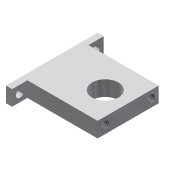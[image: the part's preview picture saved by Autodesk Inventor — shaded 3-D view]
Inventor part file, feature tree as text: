
AUTODESK INVENTOR PART (.ipt)
format: ipt  version: 2014 SP2 (Build 180246200, 246)  size: 131,072 bytes
history: native  units: in
note: dims shown in document units (in); Inventor stores cm internally (conversion verified against a paired STEP export)
features: extrude x7, sketch x7, thread x2
ambient origin geometry x8: Origin, YZ Plane, XZ Plane, XY Plane, X Axis, Y Axis, Z Axis, Center Point
bodies: Solid1 (feature_tree)
feature tree (16):
  extrude  "Extrusion1"  Depth=2.0in
  extrude  "Extrusion3"  Depth=0.5in
  extrude  "Extrusion4"  Depth=0.2in
  extrude  "Extrusion5"  Depth=0.2in
  extrude  "Extrusion6"  Depth=0.5in
  thread  "Thread1"  [1 undecoded]
  thread  "Thread2"  [1 undecoded]
  extrude  "Extrusion7"  Depth=0.75in
  extrude  "Extrusion8"  Depth=1.0in
  sketch  "Sketch1"  dims[d0=2.5in d1=2.0in]
  sketch  "Sketch3"  dims[d2=0.5in d3=0.0in d9=0.859in]
  sketch  "Sketch4"  dims[d10=1.0in d11=0.0in d12=0.2in]
  sketch  "Sketch5"  dims[d13=0.5in d14=0.0in d15=0.2in]
  sketch  "Sketch6"  dims[d16=0.5in d17=0.0in d18=0.25in d19=0.25in d20=0.25in]
  sketch  "Sketch7"  dims[d21=0.25in d22=0.75in]
  sketch  "Sketch8"  dims[d23=2.0in d24=1.0in d25=1.5in d26=0.0in d27=1.0in d28=0.0in d29=1.0in d30=0.0in d31=0.25in d32=1.5in d33=0.0in d34=0.25in d35=1.5in d36=0.0in]
note: 2 required parameter values undecoded (feature->parameter linkage not recoverable at this tier; creation-order binding heuristic only, values carry confidence <= 0.55)
